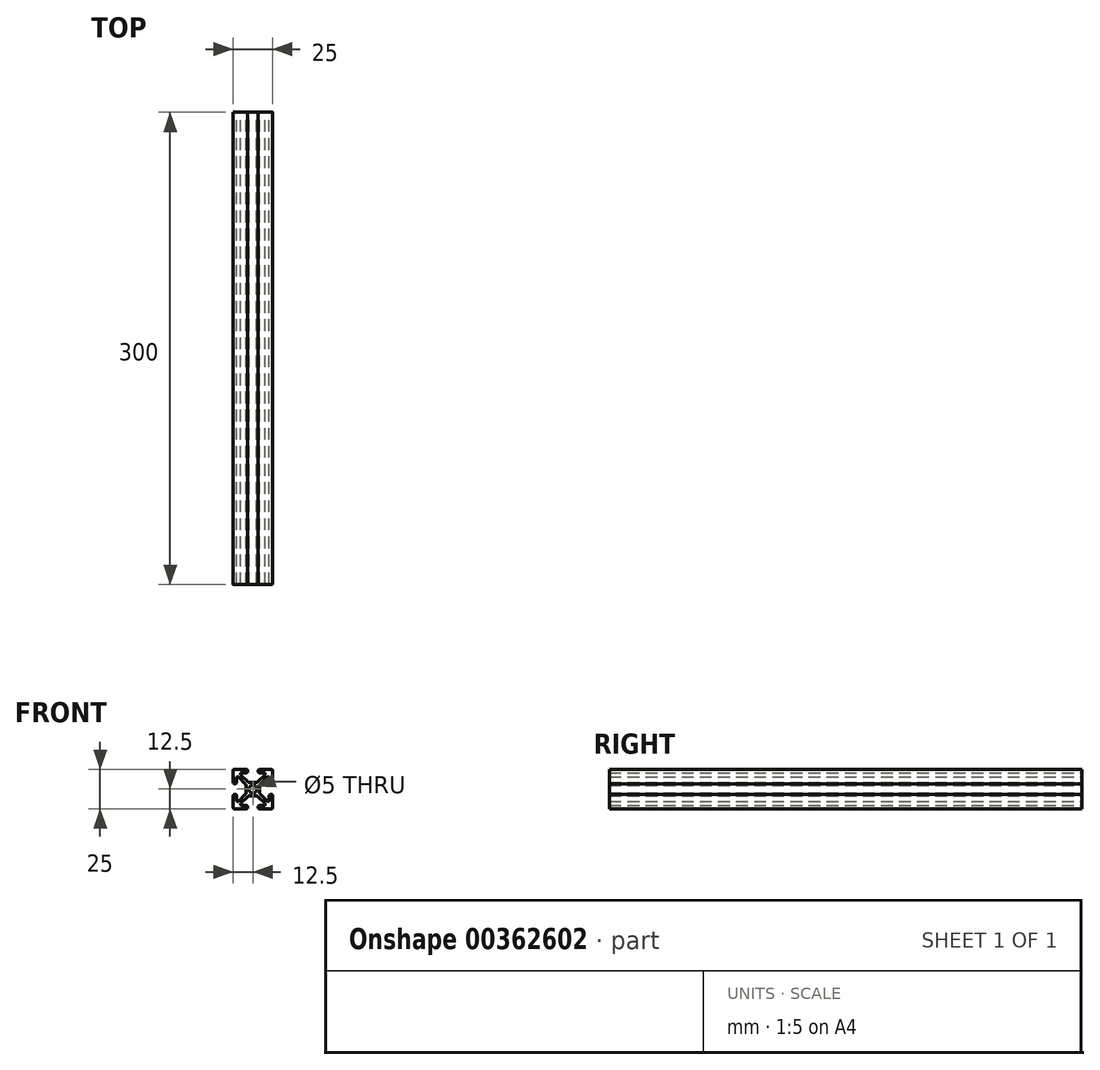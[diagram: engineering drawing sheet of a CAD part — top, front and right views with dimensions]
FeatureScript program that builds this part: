
annotation { "Feature Type Name" : "Feature", "Feature Type Description" : "" }
export const myFeature = defineFeature(function(context is Context, id is Id, definition is map)
    precondition{}
    {
        {
            var Q0;
            Q0=qCreatedBy(makeId("Front.planeOp"),FACE);
            var sketch = newSketch(context, id + "F0", { "sketchPlane" : qUnion([Q0])});
            skCircle(sketch, "E0", {"center": v(0, 0) * mm, "radius": 2.5 * mm});
            skLineSegment(sketch, "E1.bottom", {"start": v(11.8, 12.5) * mm, "end": v(4.31, 12.5) * mm});
            skLineSegment(sketch, "E1.top", {"start": v(11.8, -12.5) * mm, "end": v(4.31, -12.5) * mm});
            skLineSegment(sketch, "E1.left", {"start": v(12.5, 11.8) * mm, "end": v(12.5, 4.31) * mm});
            skLineSegment(sketch, "E1.right", {"start": v(-12.5, 11.8) * mm, "end": v(-12.5, 4.31) * mm});
            skLineSegment(sketch, "E2.bottom", {"start": v(2.58, 4.38) * mm, "end": v(-2.58, 4.38) * mm});
            skLineSegment(sketch, "E2.top", {"start": v(2.58, -4.38) * mm, "end": v(-2.58, -4.38) * mm});
            skLineSegment(sketch, "E2.left", {"start": v(4.38, 2.58) * mm, "end": v(4.38, -2.58) * mm});
            skLineSegment(sketch, "E2.right", {"start": v(-4.38, 2.58) * mm, "end": v(-4.38, -2.58) * mm});
            skLineSegment(sketch, "E3.bottom", {"start": v(-7.17, 10.37) * mm, "end": v(-4.31, 10.37) * mm});
            skLineSegment(sketch, "E3.top", {"start": v(-7.17, -10.37) * mm, "end": v(-4.31, -10.37) * mm});
            skLineSegment(sketch, "E3.left", {"start": v(-10.37, 7.17) * mm, "end": v(-10.37, 4.31) * mm});
            skLineSegment(sketch, "E3.right", {"start": v(10.37, 7.17) * mm, "end": v(10.37, 4.31) * mm});
            skLineSegment(sketch, "E4.0", {"start": v(-3.25, 11.44) * mm, "end": v(-3.25, 11.44) * mm});
            skLineSegment(sketch, "E5.0", {"start": v(3.25, 11.44) * mm, "end": v(3.25, 11.44) * mm});
            skArc(sketch, "E6", {"start": v(-4.31, 10.37) * mm, "mid": v(-3.25, 11.43) * mm, "end": v(-4.31, 12.5) * mm});
            skPoint(sketch, "E6.first.point", {"position": v(-4.31, 12.5) * mm});
            skPoint(sketch, "E6.second.point", {"position": v(-3.25, 11.44) * mm});
            skPoint(sketch, "E6.third.point", {"position": v(-4.31, 10.37) * mm});
            skArc(sketch, "E7", {"start": v(4.31, 12.5) * mm, "mid": v(3.25, 11.44) * mm, "end": v(4.31, 10.37) * mm});
            skPoint(sketch, "E7.first.point", {"position": v(4.31, 10.37) * mm});
            skPoint(sketch, "E7.second.point", {"position": v(3.25, 11.44) * mm});
            skPoint(sketch, "E7.third.point", {"position": v(4.31, 12.5) * mm});
            skArc(sketch, "E8", {"start": v(10.37, 4.31) * mm, "mid": v(11.43, 3.25) * mm, "end": v(12.5, 4.31) * mm});
            skPoint(sketch, "E8.first.point", {"position": v(10.37, 4.31) * mm});
            skPoint(sketch, "E8.second.point", {"position": v(11.45, 3.25) * mm});
            skPoint(sketch, "E8.third.point", {"position": v(12.5, 4.31) * mm});
            skArc(sketch, "E9", {"start": v(12.5, -4.31) * mm, "mid": v(11.44, -3.25) * mm, "end": v(10.37, -4.31) * mm});
            skPoint(sketch, "E9.first.point", {"position": v(12.5, -4.31) * mm});
            skPoint(sketch, "E9.second.point", {"position": v(11.4, -3.25) * mm});
            skPoint(sketch, "E9.third.point", {"position": v(10.37, -4.31) * mm});
            skLineSegment(sketch, "E10.trimOffspring", {"start": v(-4.31, 12.5) * mm, "end": v(-11.8, 12.5) * mm});
            skLineSegment(sketch, "E11.trimOffspring", {"start": v(4.31, 10.37) * mm, "end": v(7.17, 10.37) * mm});
            skLineSegment(sketch, "E12.trimOffspring", {"start": v(12.5, -4.31) * mm, "end": v(12.5, -11.8) * mm});
            skLineSegment(sketch, "E13.trimOffspring", {"start": v(10.37, -4.31) * mm, "end": v(10.37, -7.17) * mm});
            skLineSegment(sketch, "E14.0", {"start": v(4.59, -3.08) * mm, "end": v(9.18, -7.67) * mm});
            skLineSegment(sketch, "E15.0", {"start": v(3.08, -4.59) * mm, "end": v(7.67, -9.18) * mm});
            skLineSegment(sketch, "E16.1.0", {"start": v(-3.08, -4.59) * mm, "end": v(-7.67, -9.18) * mm});
            skLineSegment(sketch, "E16.1.1", {"start": v(-4.59, -3.08) * mm, "end": v(-9.18, -7.67) * mm});
            skLineSegment(sketch, "E16.2.0", {"start": v(-4.59, 3.08) * mm, "end": v(-9.18, 7.67) * mm});
            skLineSegment(sketch, "E16.2.1", {"start": v(-3.08, 4.59) * mm, "end": v(-7.67, 9.18) * mm});
            skLineSegment(sketch, "E16.3.0", {"start": v(3.08, 4.59) * mm, "end": v(7.67, 9.18) * mm});
            skLineSegment(sketch, "E16.3.1", {"start": v(4.59, 3.08) * mm, "end": v(9.18, 7.67) * mm});
            skPoint(sketch, "E17.endSnap0", {"position": v(4.38, 0) * mm});
            skPoint(sketch, "E18.newPointA", {"position": v(-10.37, 10.37) * mm});
            skArc(sketch, "E18.filletArc", {"start": v(-9.18, 7.67) * mm, "mid": v(-9.94, 7.82) * mm, "end": v(-10.37, 7.17) * mm});
            skArc(sketch, "E19.filletArc", {"start": v(10.37, 7.17) * mm, "mid": v(9.94, 7.82) * mm, "end": v(9.18, 7.67) * mm});
            skPoint(sketch, "E20.newPointB", {"position": v(10.37, 10.37) * mm});
            skArc(sketch, "E20.filletArc", {"start": v(7.67, 9.18) * mm, "mid": v(7.82, 9.94) * mm, "end": v(7.17, 10.37) * mm});
            skArc(sketch, "E21.filletArc", {"start": v(9.18, -7.67) * mm, "mid": v(9.94, -7.82) * mm, "end": v(10.37, -7.17) * mm});
            skPoint(sketch, "E22.newPointA", {"position": v(10.37, -10.37) * mm});
            skArc(sketch, "E22.filletArc", {"start": v(7.17, -10.37) * mm, "mid": v(7.82, -9.94) * mm, "end": v(7.67, -9.18) * mm});
            skPoint(sketch, "E23.newPointB", {"position": v(-10.37, -10.37) * mm});
            skArc(sketch, "E23.filletArc", {"start": v(-7.67, -9.18) * mm, "mid": v(-7.82, -9.94) * mm, "end": v(-7.17, -10.37) * mm});
            skArc(sketch, "E24.filletArc", {"start": v(-10.37, -7.17) * mm, "mid": v(-9.94, -7.82) * mm, "end": v(-9.18, -7.67) * mm});
            skArc(sketch, "E25.filletArc", {"start": v(-7.17, 10.37) * mm, "mid": v(-7.82, 9.94) * mm, "end": v(-7.67, 9.18) * mm});
            skPoint(sketch, "E26.newPointB", {"position": v(-4.38, 4.38) * mm});
            skArc(sketch, "E26.filletArc", {"start": v(-4.38, 2.58) * mm, "mid": v(-4.43, 2.85) * mm, "end": v(-4.59, 3.08) * mm});
            skPoint(sketch, "E27.newPointB", {"position": v(-4.38, -4.38) * mm});
            skArc(sketch, "E27.filletArc", {"start": v(-4.59, -3.08) * mm, "mid": v(-4.43, -2.85) * mm, "end": v(-4.38, -2.58) * mm});
            skArc(sketch, "E28.filletArc", {"start": v(-3.08, 4.59) * mm, "mid": v(-2.85, 4.43) * mm, "end": v(-2.58, 4.38) * mm});
            skPoint(sketch, "E29.newPointA", {"position": v(4.38, 4.38) * mm});
            skArc(sketch, "E29.filletArc", {"start": v(2.58, 4.38) * mm, "mid": v(2.85, 4.43) * mm, "end": v(3.08, 4.59) * mm});
            skArc(sketch, "E30.filletArc", {"start": v(4.59, 3.08) * mm, "mid": v(4.43, 2.85) * mm, "end": v(4.38, 2.58) * mm});
            skPoint(sketch, "E31.newPointA", {"position": v(4.38, -4.38) * mm});
            skArc(sketch, "E31.filletArc", {"start": v(4.38, -2.58) * mm, "mid": v(4.43, -2.85) * mm, "end": v(4.59, -3.08) * mm});
            skArc(sketch, "E32.filletArc", {"start": v(3.08, -4.59) * mm, "mid": v(2.85, -4.43) * mm, "end": v(2.58, -4.38) * mm});
            skArc(sketch, "E33.filletArc", {"start": v(-2.58, -4.38) * mm, "mid": v(-2.85, -4.43) * mm, "end": v(-3.08, -4.59) * mm});
            skPoint(sketch, "E34.visualSharp", {"position": v(12.5, 12.5) * mm});
            skArc(sketch, "E34.filletArc", {"start": v(12.5, 11.8) * mm, "mid": v(12.3, 12.3) * mm, "end": v(11.8, 12.5) * mm});
            skPoint(sketch, "E35.visualSharp", {"position": v(-12.5, 12.5) * mm});
            skArc(sketch, "E35.filletArc", {"start": v(-11.8, 12.5) * mm, "mid": v(-12.3, 12.3) * mm, "end": v(-12.5, 11.8) * mm});
            skPoint(sketch, "E36.visualSharp", {"position": v(-12.5, -12.5) * mm});
            skArc(sketch, "E36.filletArc", {"start": v(-12.5, -11.8) * mm, "mid": v(-12.3, -12.3) * mm, "end": v(-11.8, -12.5) * mm});
            skPoint(sketch, "E37.visualSharp", {"position": v(12.5, -12.5) * mm});
            skArc(sketch, "E37.filletArc", {"start": v(11.8, -12.5) * mm, "mid": v(12.3, -12.3) * mm, "end": v(12.5, -11.8) * mm});
            skArc(sketch, "E38.MirrorCS", {"start": v(4.31, -12.5) * mm, "mid": v(3.25, -11.44) * mm, "end": v(4.31, -10.37) * mm});
            skArc(sketch, "E39.MirrorCS", {"start": v(-4.31, -10.37) * mm, "mid": v(-3.25, -11.43) * mm, "end": v(-4.31, -12.5) * mm});
            skArc(sketch, "E40.MirrorCS", {"start": v(10.37, -4.31) * mm, "mid": v(11.43, -3.25) * mm, "end": v(12.5, -4.31) * mm});
            skArc(sketch, "E41.MirrorCS", {"start": v(12.5, 4.31) * mm, "mid": v(11.44, 3.25) * mm, "end": v(10.37, 4.31) * mm});
            skArc(sketch, "E42.MirrorCS", {"start": v(-10.37, 4.31) * mm, "mid": v(-11.43, 3.25) * mm, "end": v(-12.5, 4.31) * mm});
            skArc(sketch, "E43.MirrorCS", {"start": v(-12.5, -4.31) * mm, "mid": v(-11.44, -3.25) * mm, "end": v(-10.37, -4.31) * mm});
            skLineSegment(sketch, "E44.trimOffspring", {"start": v(4.31, -10.37) * mm, "end": v(7.17, -10.37) * mm});
            skLineSegment(sketch, "E45.trimOffspring", {"start": v(-4.31, -12.5) * mm, "end": v(-11.8, -12.5) * mm});
            skLineSegment(sketch, "E46.trimOffspring", {"start": v(-10.37, -4.31) * mm, "end": v(-10.37, -7.17) * mm});
            skLineSegment(sketch, "E47.trimOffspring", {"start": v(-12.5, -4.31) * mm, "end": v(-12.5, -11.8) * mm});
            skSolve(sketch);
        }
        {
            var Q0;
            Q0 = qSketchRegion(id + "F0", true);
            extrude(context, id + "F1", {"entities" : qUnion([Q0]), "depth" : 300 * mm});
        }
    });
